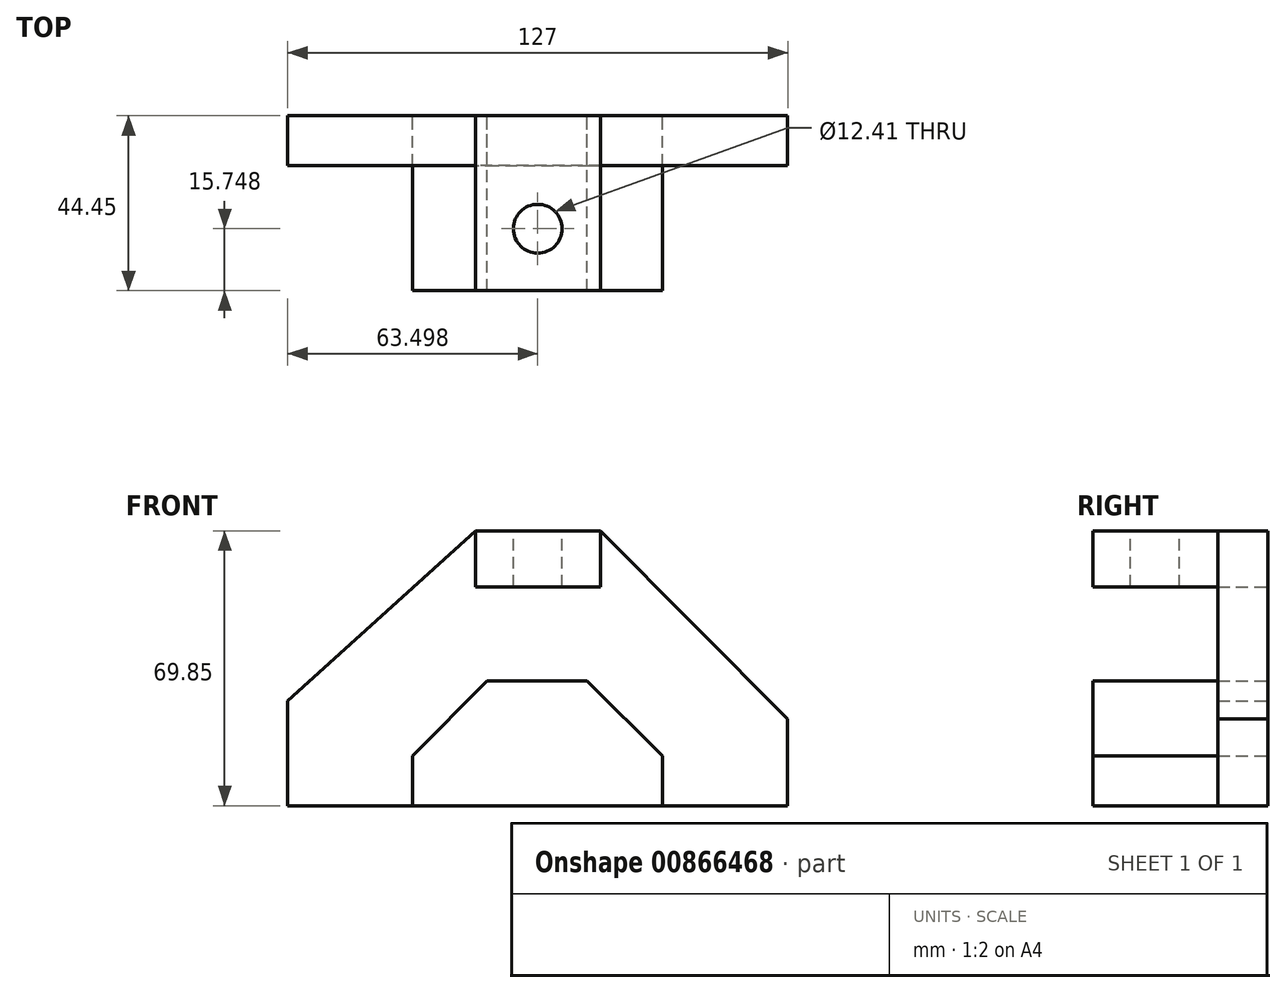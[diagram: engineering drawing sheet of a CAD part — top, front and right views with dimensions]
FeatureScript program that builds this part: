
annotation { "Feature Type Name" : "Feature", "Feature Type Description" : "" }
export const myFeature = defineFeature(function(context is Context, id is Id, definition is map)
    precondition{}
    {
        {
            var Q0;
            Q0=qCreatedBy(makeId("Front.planeOp"),FACE);
            var sketch = newSketch(context, id + "F0", { "sketchPlane" : qUnion([Q0])});
            skLineSegment(sketch, "E0", {"start": v(-69.85, 12.27) * mm, "end": v(-69.85, -14.4) * mm});
            skLineSegment(sketch, "E1", {"start": v(-69.85, -14.4) * mm, "end": v(57.15, -14.4) * mm});
            skLineSegment(sketch, "E2", {"start": v(57.15, -14.4) * mm, "end": v(57.15, 7.7) * mm});
            skLineSegment(sketch, "E3", {"start": v(57.15, 7.7) * mm, "end": v(9.65, 55.45) * mm});
            skLineSegment(sketch, "E4", {"start": v(9.65, 55.45) * mm, "end": v(-22.1, 55.45) * mm});
            skLineSegment(sketch, "E5", {"start": v(-22.1, 55.45) * mm, "end": v(-69.85, 12.27) * mm});
            skLineSegment(sketch, "E6", {"start": v(9.65, 55.45) * mm, "end": v(9.65, 41.23) * mm});
            skLineSegment(sketch, "E7", {"start": v(9.65, 41.23) * mm, "end": v(-22.1, 41.23) * mm});
            skLineSegment(sketch, "E8", {"start": v(-22.1, 41.23) * mm, "end": v(-22.1, 55.45) * mm});
            skLineSegment(sketch, "E9", {"start": v(-38.1, -14.4) * mm, "end": v(-38.1, -1.7) * mm});
            skLineSegment(sketch, "E10", {"start": v(-38.1, -1.7) * mm, "end": v(-19.19, 17.35) * mm});
            skLineSegment(sketch, "E11", {"start": v(-19.19, 17.35) * mm, "end": v(6.21, 17.35) * mm});
            skLineSegment(sketch, "E12", {"start": v(6.21, 17.35) * mm, "end": v(25.4, -1.7) * mm});
            skLineSegment(sketch, "E13", {"start": v(25.4, -1.7) * mm, "end": v(25.4, -14.4) * mm});
            skSolve(sketch);
        }
        {
            var Q0;
            {var subQ0=sQuery(id+"F0.wireOp",EDGE,"E9");Q0=makeQuery(id+"F0.imprint","IMPRINT",FACE,{"disambiguationData":[TD([[makeQuery(id+"F0.imprint","IMPRINT",EDGE,{"derivedFrom":subQ0}),-1.0]])]});}
            var Q1;
            Q1=makeQuery(id+"F0.imprint","IMPRINT",FACE,{"disambiguationData":[TD([[makeQuery(id+"F0.imprint","IMPRINT",EDGE,{"derivedFrom":sQuery(id+"F0.wireOp",EDGE,"E4")}),1.0]])]});
            extrude(context, id + "F1", {"entities" : qUnion([Q0, Q1]), "depth" : 44.45 * mm, "offsetDistance" : 25.4 * mm});
        }
        {
            var Q0;
            {var subQ1=sQuery(id+"F0.wireOp",EDGE,"E0");Q0=makeQuery(id+"F0.imprint","IMPRINT",FACE,{"disambiguationData":[TD([[makeQuery(id+"F0.imprint","IMPRINT",EDGE,{"derivedFrom":subQ1}),1.0]])]});}
            extrude(context, id + "F2", {"entities" : qUnion([Q0]), "depth" : 12.7 * mm, "offsetDistance" : 25.4 * mm});
        }
        {
            var Q0;
            Q0=makeQuery(id+"F1.opExtrude","SWEPT_FACE",FACE,{"disambiguationData":[OSD([sQuery(id+"F0.wireOp",EDGE,"E4")])]});
            var sketch = newSketch(context, id + "F3", { "sketchPlane" : qUnion([Q0])});
            skCircle(sketch, "E14", {"center": v(-6.35, -28.7) * mm, "radius": 6.2 * mm});
            skSolve(sketch);
        }
        {
            var Q0;
            Q0=makeQuery(id+"F3.imprint","IMPRINT",FACE,{"disambiguationData":[TD([[makeQuery(id+"F3.imprint","IMPRINT",EDGE,{"derivedFrom":sQuery(id+"F3.wireOp",EDGE,"E14")}),1.0]])]});
            extrude(context, id + "F4", {"entities" : qUnion([Q0]), "operationType" : NewBodyOperationType.REMOVE, "oppositeDirection" : true, "depth" : 25.4 * mm, "offsetDistance" : 25.4 * mm});
        }
    });
